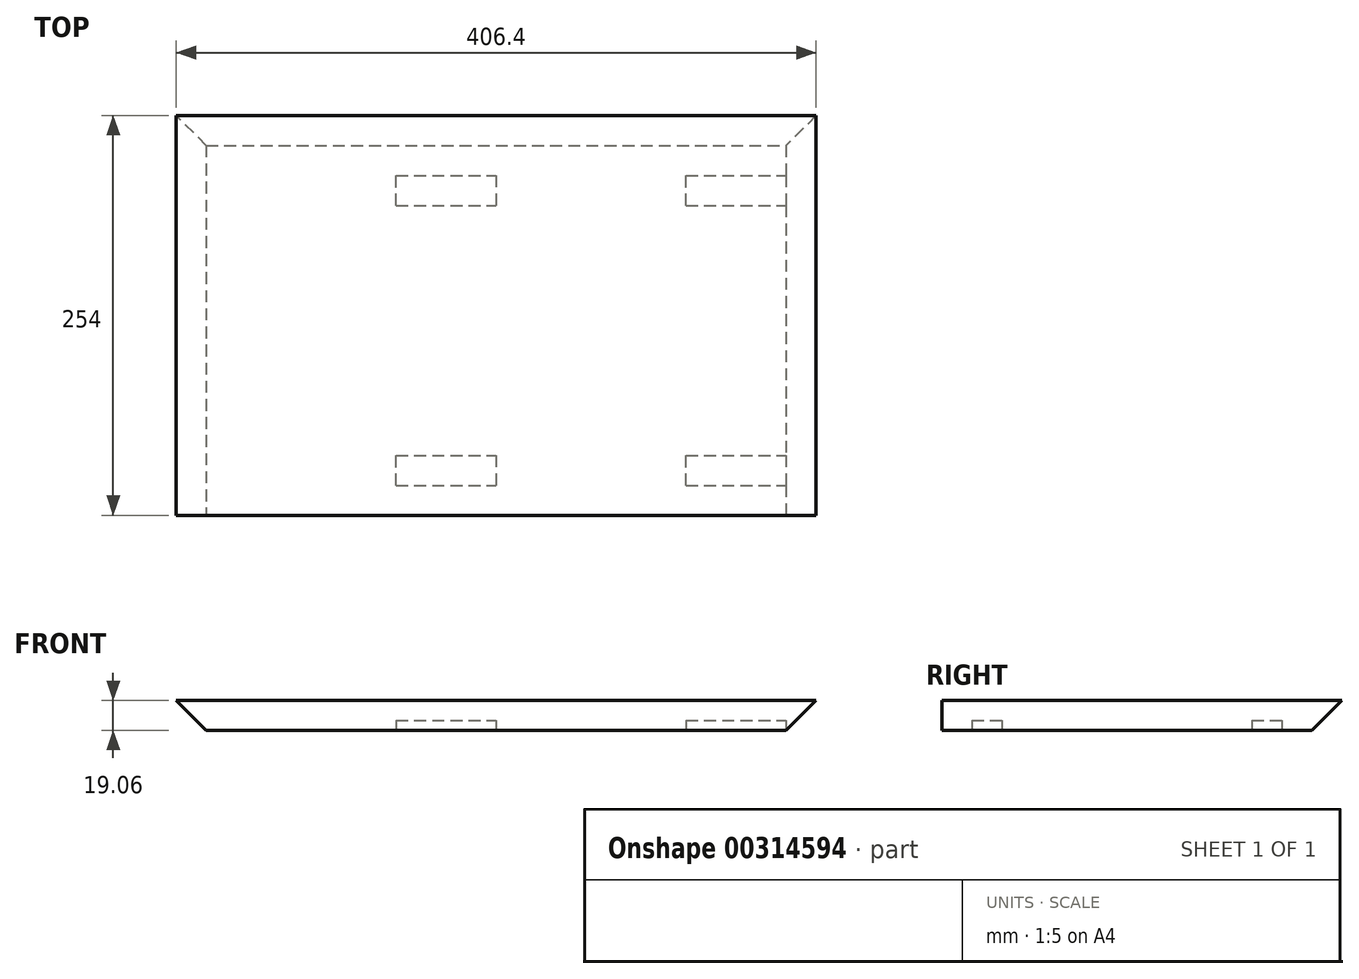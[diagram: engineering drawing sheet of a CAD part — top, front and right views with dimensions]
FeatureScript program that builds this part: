
annotation { "Feature Type Name" : "Feature", "Feature Type Description" : "" }
export const myFeature = defineFeature(function(context is Context, id is Id, definition is map)
    precondition{}
    {
        {
            var Q0;
            Q0=qCreatedBy(makeId("Front.planeOp"),FACE);
            var sketch = newSketch(context, id + "F0", { "sketchPlane" : qUnion([Q0])});
            skLineSegment(sketch, "E0", {"start": v(-203.2, 9.52) * mm, "end": v(203.2, 9.52) * mm});
            skLineSegment(sketch, "E1", {"start": v(203.2, 9.52) * mm, "end": v(184.15, -9.53) * mm});
            skLineSegment(sketch, "E2", {"start": v(184.15, -9.53) * mm, "end": v(-184.15, -9.53) * mm});
            skLineSegment(sketch, "E3", {"start": v(-184.15, -9.53) * mm, "end": v(-203.2, 9.53) * mm});
            skLineSegment(sketch, "E4", {"start": v(0, 9.53) * mm, "end": v(0, -9.53) * mm, "construction": true});
            skSolve(sketch);
        }
        {
            var Q0;
            Q0=qSketchRegion(id+"F0",true);
            extrude(context, id + "F1", {"entities" : qUnion([Q0]), "oppositeDirection" : true, "depth" : 254 * mm});
        }
        {
            var Q0;
            Q0=makeQuery(id+"F1.opExtrude","CAP_EDGE",EDGE,{"disambiguationData":[OSD([sQuery(id+"F0.wireOp",EDGE,"E2")])],"isStart":false});
            chamfer(context, id + "F2", {"entities" : qUnion([Q0]), "width" : 19.05 * mm, "tangentPropagation" : true});
        }
        {
            var Q0;
            Q0=makeQuery(id+"F1.opExtrude","SWEPT_FACE",FACE,{"disambiguationData":[OSD([sQuery(id+"F0.wireOp",EDGE,"E2")])]});
            var sketch = newSketch(context, id + "F3", { "sketchPlane" : qUnion([Q0])});
            skLineSegment(sketch, "E5", {"start": v(-184.15, -19.05) * mm, "end": v(184.15, -19.05) * mm});
            skLineSegment(sketch, "E6", {"start": v(-184.15, -38.1) * mm, "end": v(184.15, -38.1) * mm});
            skLineSegment(sketch, "E7", {"start": v(-184.15, -215.9) * mm, "end": v(184.15, -215.9) * mm});
            skLineSegment(sketch, "E8", {"start": v(-184.15, -196.85) * mm, "end": v(184.15, -196.85) * mm});
            skLineSegment(sketch, "E9", {"start": v(120.65, 0) * mm, "end": v(120.65, -234.95) * mm});
            skLineSegment(sketch, "E10", {"start": v(-63.5, 0) * mm, "end": v(-63.5, -234.95) * mm});
            skLineSegment(sketch, "E11", {"start": v(0, -234.95) * mm, "end": v(0, 0) * mm});
            skSolve(sketch);
        }
        {
            var Q0;
            {var subQ0=sQuery(id+"F3.wireOp",EDGE,"E10");var subQ1=sQuery(id+"F3.wireOp",EDGE,"E7");var subQ2=makeQuery(id+"F3.imprint","INTERSECT",VERTEX,{"derivedFrom":[subQ1,subQ0]});Q0=makeQuery(id+"F3.imprint","IMPRINT",FACE,{"disambiguationData":[TD([[makeQuery(id+"F3.imprint","IMPRINT",EDGE,{"disambiguationData":[TD([[subQ2,-1.0]])],"derivedFrom":subQ1}),1.0]])]});}
            var Q1;
            {var subQ0=sQuery(id+"F3.wireOp",EDGE,"E10");var subQ1=sQuery(id+"F3.wireOp",EDGE,"E5");var subQ2=makeQuery(id+"F3.imprint","INTERSECT",VERTEX,{"derivedFrom":[subQ1,subQ0]});Q1=makeQuery(id+"F3.imprint","IMPRINT",FACE,{"disambiguationData":[TD([[makeQuery(id+"F3.imprint","IMPRINT",EDGE,{"disambiguationData":[TD([[subQ2,-1.0]])],"derivedFrom":subQ1}),-1.0]])]});}
            var Q2;
            {var subQ0=sQuery(id+"F3.wireOp",EDGE,"E5");var subQ3=sQuery(id+"F3.wireOp",EDGE,"E9");var subQ4=makeQuery(id+"F3.imprint","INTERSECT",VERTEX,{"derivedFrom":[subQ0,subQ3]});Q2=makeQuery(id+"F3.imprint","IMPRINT",FACE,{"disambiguationData":[TD([[makeQuery(id+"F3.imprint","IMPRINT",EDGE,{"disambiguationData":[TD([[subQ4,-1.0]])],"derivedFrom":subQ3}),1.0]])]});}
            var Q3;
            {var subQ0=sQuery(id+"F3.wireOp",EDGE,"E7");var subQ3=sQuery(id+"F3.wireOp",EDGE,"E9");var subQ4=makeQuery(id+"F3.imprint","INTERSECT",VERTEX,{"derivedFrom":[subQ0,subQ3]});Q3=makeQuery(id+"F3.imprint","IMPRINT",FACE,{"disambiguationData":[TD([[makeQuery(id+"F3.imprint","IMPRINT",EDGE,{"disambiguationData":[TD([[subQ4,1.0]])],"derivedFrom":subQ3}),1.0]])]});}
            extrude(context, id + "F4", {"entities" : qUnion([Q0, Q1, Q2, Q3]), "operationType" : NewBodyOperationType.REMOVE, "oppositeDirection" : true, "depth" : 6.35 * mm});
        }
    });
